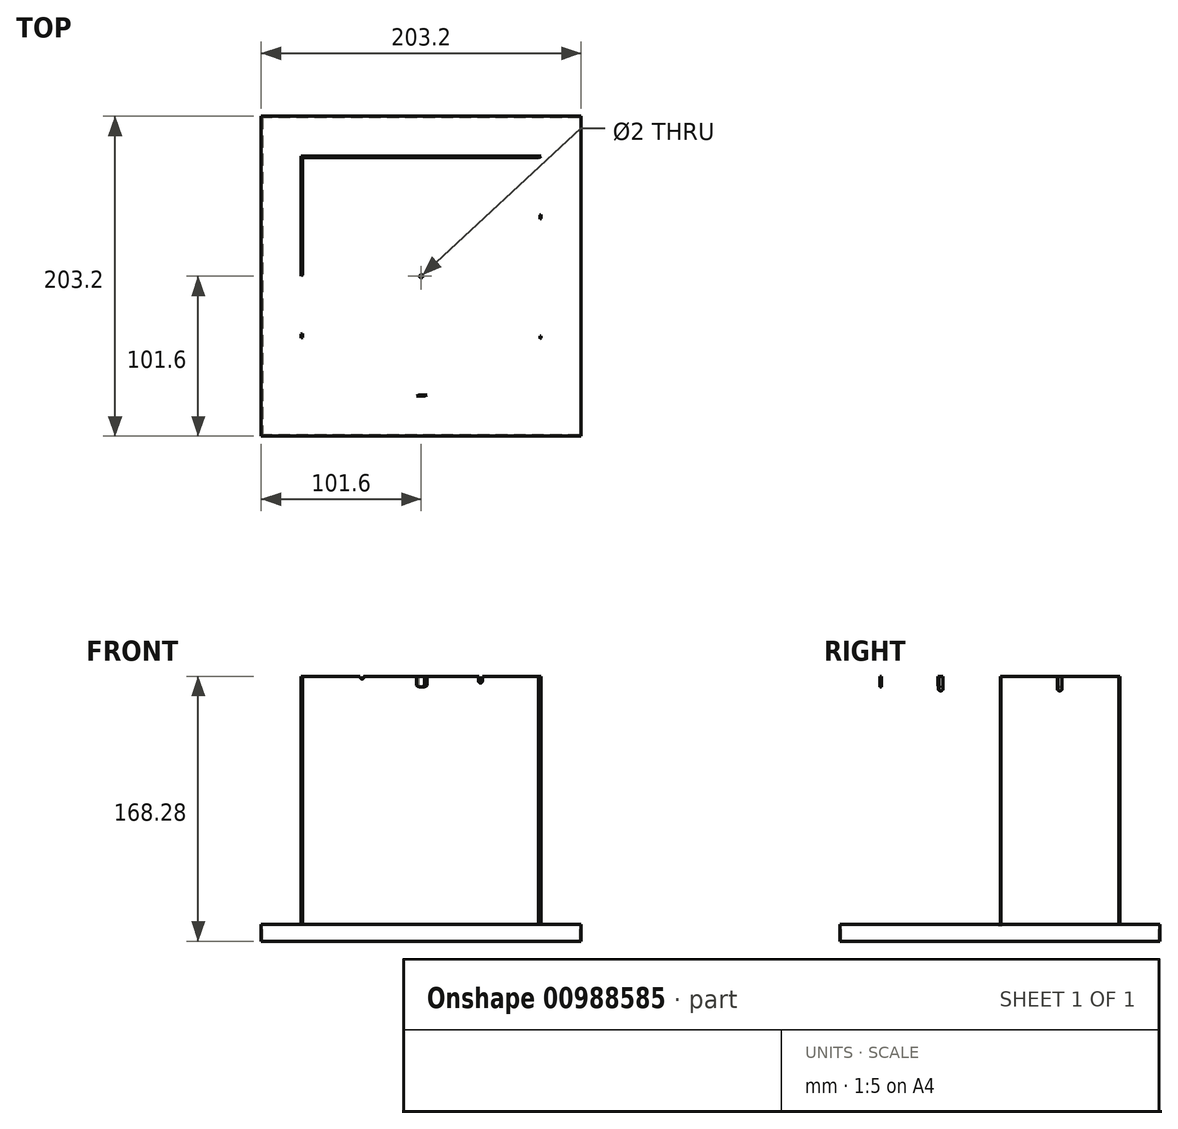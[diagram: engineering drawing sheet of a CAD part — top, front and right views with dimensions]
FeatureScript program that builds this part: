
annotation { "Feature Type Name" : "Feature", "Feature Type Description" : "" }
export const myFeature = defineFeature(function(context is Context, id is Id, definition is map)
    precondition{}
    {
        {
            var Q0;
            Q0=qCreatedBy(makeId("Top.planeOp"),FACE);
            var sketch = newSketch(context, id + "F0", { "sketchPlane" : qUnion([Q0])});
            skLineSegment(sketch, "E0.bottom", {"start": v(101.6, 101.6) * mm, "end": v(-101.6, 101.6) * mm});
            skLineSegment(sketch, "E0.top", {"start": v(101.6, -101.6) * mm, "end": v(-101.6, -101.6) * mm});
            skLineSegment(sketch, "E0.left", {"start": v(101.6, 101.6) * mm, "end": v(101.6, -101.6) * mm});
            skLineSegment(sketch, "E0.right", {"start": v(-101.6, 101.6) * mm, "end": v(-101.6, -101.6) * mm});
            skPoint(sketch, "E0.middle", {"position": v(0, 0) * mm});
            skCircle(sketch, "E1", {"center": v(0, 0) * mm, "radius": 1 * mm});
            skSolve(sketch);
        }
        {
            var Q0;
            Q0=makeQuery(id+"F0.imprint","IMPRINT",FACE,{"disambiguationData":[TD([[makeQuery(id+"F0.imprint","IMPRINT",EDGE,{"derivedFrom":sQuery(id+"F0.wireOp",EDGE,"E0.bottom")}),1.0]])]});
            extrude(context, id + "F1", {"entities" : qUnion([Q0]), "depth" : 0.8 * mm, "offsetDistance" : 25.4 * mm});
        }
        {
            var Q0;
            Q0=makeQuery(id+"F1.opExtrude","CAP_FACE",FACE,{"disambiguationData":[OSD([sQuery(id+"F0.wireOp",EDGE,"E0.bottom"),sQuery(id+"F0.wireOp",EDGE,"E0.top"),sQuery(id+"F0.wireOp",EDGE,"E0.left"),sQuery(id+"F0.wireOp",EDGE,"E0.right")])],"isStart":true});
            var sketch = newSketch(context, id + "F2", { "sketchPlane" : qUnion([Q0])});
            skLineSegment(sketch, "E2.0", {"start": v(-101.6, -101.6) * mm, "end": v(-101.6, 101.6) * mm});
            skLineSegment(sketch, "E2.1", {"start": v(101.6, 101.6) * mm, "end": v(-101.6, 101.6) * mm});
            skLineSegment(sketch, "E2.2", {"start": v(101.6, -101.6) * mm, "end": v(101.6, 101.6) * mm});
            skLineSegment(sketch, "E2.3", {"start": v(101.6, -101.6) * mm, "end": v(-101.6, -101.6) * mm});
            skLineSegment(sketch, "E3.0", {"start": v(-100.8, -100.8) * mm, "end": v(-100.8, 100.8) * mm});
            skLineSegment(sketch, "E3.1", {"start": v(100.8, -100.8) * mm, "end": v(-100.8, -100.8) * mm});
            skLineSegment(sketch, "E3.2", {"start": v(100.8, -100.8) * mm, "end": v(100.8, 100.8) * mm});
            skLineSegment(sketch, "E3.3", {"start": v(100.8, 100.8) * mm, "end": v(-100.8, 100.8) * mm});
            skSolve(sketch);
        }
        {
            var Q0;
            Q0 = qSketchRegion(id + "F2", true);
            extrude(context, id + "F3", {"entities" : qUnion([Q0]), "operationType" : NewBodyOperationType.ADD, "depth" : 10 * mm, "offsetDistance" : 25.4 * mm});
        }
        {
            var Q0;
            Q0=makeQuery(id+"F1.opExtrude","CAP_FACE",FACE,{"disambiguationData":[OSD([sQuery(id+"F0.wireOp",EDGE,"E0.bottom"),sQuery(id+"F0.wireOp",EDGE,"E0.top"),sQuery(id+"F0.wireOp",EDGE,"E0.left"),sQuery(id+"F0.wireOp",EDGE,"E0.right")])],"isStart":false});
            var sketch = newSketch(context, id + "F4", { "sketchPlane" : qUnion([Q0])});
            skLineSegment(sketch, "E4.bottom", {"start": v(76.2, 76.2) * mm, "end": v(-76.2, 76.2) * mm});
            skLineSegment(sketch, "E4.top", {"start": v(76.2, -76.2) * mm, "end": v(-76.2, -76.2) * mm});
            skLineSegment(sketch, "E4.left", {"start": v(76.2, 76.2) * mm, "end": v(76.2, -76.2) * mm});
            skLineSegment(sketch, "E4.right", {"start": v(-76.2, 76.2) * mm, "end": v(-76.2, -76.2) * mm});
            skPoint(sketch, "E4.middle", {"position": v(0, 0) * mm});
            skLineSegment(sketch, "E5.0", {"start": v(-75.4, 75.4) * mm, "end": v(-75.4, -75.4) * mm});
            skLineSegment(sketch, "E5.1", {"start": v(75.4, 75.4) * mm, "end": v(-75.4, 75.4) * mm});
            skLineSegment(sketch, "E5.2", {"start": v(75.4, 75.4) * mm, "end": v(75.4, -75.4) * mm});
            skLineSegment(sketch, "E5.3", {"start": v(75.4, -75.4) * mm, "end": v(-75.4, -75.4) * mm});
            skSolve(sketch);
        }
        {
            var Q0;
            Q0 = qSketchRegion(id + "F4", true);
            extrude(context, id + "F5", {"entities" : qUnion([Q0]), "depth" : 157.48 * mm, "offsetDistance" : 25.4 * mm});
        }
        {
            var Q0;
            Q0=makeQuery(id+"F5.opExtrude","SWEPT_FACE",FACE,{"disambiguationData":[OSD([sQuery(id+"F4.wireOp",EDGE,"E4.top")])]});
            var sketch = newSketch(context, id + "F6", { "sketchPlane" : qUnion([Q0])});
            skLineSegment(sketch, "E6", {"start": v(36.75, 158.28) * mm, "end": v(39.25, 158.28) * mm});
            skLineSegment(sketch, "E7", {"start": v(-39.25, 158.28) * mm, "end": v(-39.25, 155.28) * mm});
            skLineSegment(sketch, "E8", {"start": v(-36.75, 158.28) * mm, "end": v(-36.75, 155.28) * mm});
            skArc(sketch, "E9", {"start": v(-36.75, 155.28) * mm, "mid": v(-38, 154.03) * mm, "end": v(-39.25, 155.28) * mm});
            skLineSegment(sketch, "E10", {"start": v(-39.25, 158.28) * mm, "end": v(-36.75, 158.28) * mm});
            skLineSegment(sketch, "E11", {"start": v(36.75, 158.28) * mm, "end": v(36.75, 157.78) * mm});
            skLineSegment(sketch, "E12", {"start": v(39.25, 158.28) * mm, "end": v(39.25, 157.78) * mm});
            skArc(sketch, "E13", {"start": v(39.25, 157.78) * mm, "mid": v(38, 156.53) * mm, "end": v(36.75, 157.78) * mm});
            skSolve(sketch);
        }
        {
            var Q0;
            Q0=makeQuery(id+"F5.opExtrude","SWEPT_FACE",FACE,{"disambiguationData":[OSD([sQuery(id+"F4.wireOp",EDGE,"E4.left")])]});
            var sketch = newSketch(context, id + "F7", { "sketchPlane" : qUnion([Q0])});
            skArc(sketch, "E14", {"start": v(39.25, 150.28) * mm, "mid": v(38, 149.03) * mm, "end": v(36.75, 150.28) * mm});
            skLineSegment(sketch, "E15", {"start": v(-39.25, 158.28) * mm, "end": v(-39.25, 152.78) * mm});
            skLineSegment(sketch, "E16", {"start": v(-36.75, 158.28) * mm, "end": v(-36.75, 152.78) * mm});
            skArc(sketch, "E17", {"start": v(-36.75, 152.78) * mm, "mid": v(-38, 151.53) * mm, "end": v(-39.25, 152.78) * mm});
            skLineSegment(sketch, "E18", {"start": v(-39.25, 158.28) * mm, "end": v(-36.75, 158.28) * mm});
            skLineSegment(sketch, "E19", {"start": v(39.25, 150.28) * mm, "end": v(39.25, 158.28) * mm});
            skLineSegment(sketch, "E20", {"start": v(39.25, 158.28) * mm, "end": v(36.75, 158.28) * mm});
            skLineSegment(sketch, "E21", {"start": v(36.75, 158.28) * mm, "end": v(36.75, 150.28) * mm});
            skSolve(sketch);
        }
        {
            var Q0;
            Q0=makeQuery(id+"F5.opExtrude","CAP_FACE",FACE,{"disambiguationData":[OSD([sQuery(id+"F4.wireOp",EDGE,"E4.bottom"),sQuery(id+"F4.wireOp",EDGE,"E4.top"),sQuery(id+"F4.wireOp",EDGE,"E4.left"),sQuery(id+"F4.wireOp",EDGE,"E4.right"),sQuery(id+"F4.wireOp",EDGE,"E5.0"),sQuery(id+"F4.wireOp",EDGE,"E5.1"),sQuery(id+"F4.wireOp",EDGE,"E5.2"),sQuery(id+"F4.wireOp",EDGE,"E5.3")])],"isStart":false});
            var sketch = newSketch(context, id + "F8", { "sketchPlane" : qUnion([Q0])});
            skLineSegment(sketch, "E22", {"start": v(76.2, 38) * mm, "end": v(-76.2, -38) * mm});
            skLineSegment(sketch, "E23", {"start": v(76.2, -38) * mm, "end": v(-76.2, 38) * mm});
            skLineSegment(sketch, "E24", {"start": v(38, -76.2) * mm, "end": v(-38, 76.2) * mm});
            skLineSegment(sketch, "E25", {"start": v(-38, -76.2) * mm, "end": v(38, 76.2) * mm});
            skSolve(sketch);
        }
        {
            var Q0;
            Q0=makeQuery(id+"F6.imprint","IMPRINT",FACE,{"disambiguationData":[TD([[makeQuery(id+"F6.imprint","IMPRINT",EDGE,{"derivedFrom":sQuery(id+"F6.wireOp",EDGE,"E6")}),1.0]])]});
            var Q1;
            Q1=sQuery(id+"F8.wireOp",EDGE,"E24");
            sweep(context, id + "F9", {"operationType" : NewBodyOperationType.REMOVE, "profiles" : qUnion([Q0]), "path" : qUnion([Q1])});
        }
        {
            var Q0;
            Q0=makeQuery(id+"F6.imprint","IMPRINT",FACE,{"disambiguationData":[TD([[makeQuery(id+"F6.imprint","IMPRINT",EDGE,{"derivedFrom":sQuery(id+"F6.wireOp",EDGE,"E7")}),1.0]])]});
            var Q1;
            Q1=sQuery(id+"F8.wireOp",EDGE,"E25");
            sweep(context, id + "F10", {"operationType" : NewBodyOperationType.REMOVE, "profiles" : qUnion([Q0]), "path" : qUnion([Q1])});
        }
        {
            var Q0;
            Q0=makeQuery(id+"F7.imprint","IMPRINT",FACE,{"disambiguationData":[TD([[makeQuery(id+"F7.imprint","IMPRINT",EDGE,{"derivedFrom":sQuery(id+"F7.wireOp",EDGE,"E15")}),1.0]])]});
            var Q1;
            Q1=sQuery(id+"F8.wireOp",EDGE,"E23");
            sweep(context, id + "F11", {"operationType" : NewBodyOperationType.REMOVE, "profiles" : qUnion([Q0]), "path" : qUnion([Q1])});
        }
        {
            var Q0;
            Q0=makeQuery(id+"F7.imprint","IMPRINT",FACE,{"disambiguationData":[TD([[makeQuery(id+"F7.imprint","IMPRINT",EDGE,{"derivedFrom":sQuery(id+"F7.wireOp",EDGE,"E14")}),-1.0]])]});
            var Q1;
            Q1=sQuery(id+"F8.wireOp",EDGE,"E22");
            sweep(context, id + "F12", {"operationType" : NewBodyOperationType.REMOVE, "profiles" : qUnion([Q0]), "path" : qUnion([Q1])});
        }
    });
